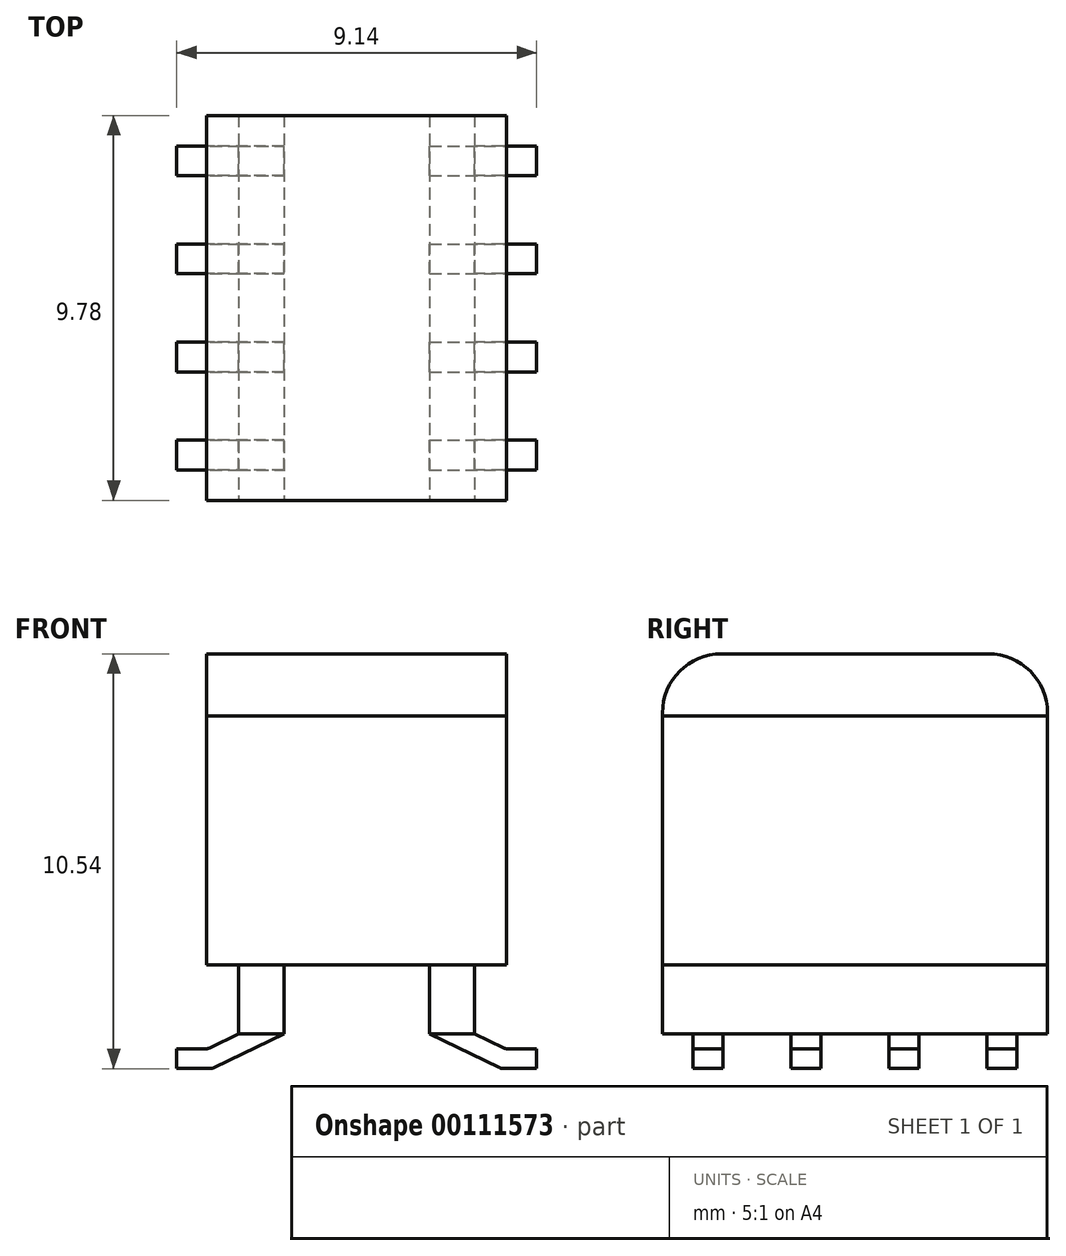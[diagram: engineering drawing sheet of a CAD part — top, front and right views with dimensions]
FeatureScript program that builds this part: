
annotation { "Feature Type Name" : "Feature", "Feature Type Description" : "" }
export const myFeature = defineFeature(function(context is Context, id is Id, definition is map)
    precondition{}
    {
        {
            var Q0;
            Q0=qCreatedBy(makeId("Top.planeOp"),FACE);
            var sketch = newSketch(context, id + "F0", { "sketchPlane" : qUnion([Q0])});
            skLineSegment(sketch, "E0.bottom", {"start": v(-3, 4.9) * mm, "end": v(-1.85, 4.9) * mm});
            skLineSegment(sketch, "E0.top", {"start": v(-3, -4.89) * mm, "end": v(-1.85, -4.89) * mm});
            skLineSegment(sketch, "E0.left", {"start": v(-3, 4.9) * mm, "end": v(-3, -4.89) * mm});
            skLineSegment(sketch, "E0.right", {"start": v(-1.85, 4.9) * mm, "end": v(-1.85, -4.89) * mm});
            skLineSegment(sketch, "E1.MirrorCS", {"start": v(3, -4.89) * mm, "end": v(1.85, -4.89) * mm});
            skLineSegment(sketch, "E2.MirrorCS", {"start": v(3, 4.9) * mm, "end": v(1.85, 4.9) * mm});
            skLineSegment(sketch, "E3.MirrorCS", {"start": v(3, 4.9) * mm, "end": v(3, -4.89) * mm});
            skLineSegment(sketch, "E4.MirrorCS", {"start": v(1.85, 4.9) * mm, "end": v(1.85, -4.89) * mm});
            skSolve(sketch);
        }
        {
            var Q0;
            Q0 = qSketchRegion(id + "F0", true);
            extrude(context, id + "F1", {"entities" : qUnion([Q0]), "depth" : 1.76 * mm});
        }
        {
            var Q0;
            Q0=makeQuery(id+"F1.opExtrude","CAP_FACE",FACE,{"disambiguationData":[OSD([sQuery(id+"F0.wireOp",EDGE,"E0.bottom"),sQuery(id+"F0.wireOp",EDGE,"E0.top"),sQuery(id+"F0.wireOp",EDGE,"E0.left"),sQuery(id+"F0.wireOp",EDGE,"E0.right")])],"isStart":false});
            var sketch = newSketch(context, id + "F2", { "sketchPlane" : qUnion([Q0])});
            skPoint(sketch, "E5.firstSnap0", {"position": v(-2.43, 4.9) * mm});
            skLineSegment(sketch, "E5.bottom", {"start": v(-3.81, 4.9) * mm, "end": v(3.81, 4.9) * mm});
            skLineSegment(sketch, "E5.top", {"start": v(-3.81, -4.89) * mm, "end": v(3.81, -4.89) * mm});
            skLineSegment(sketch, "E5.left", {"start": v(-3.81, 4.89) * mm, "end": v(-3.81, -4.89) * mm});
            skLineSegment(sketch, "E5.right", {"start": v(3.81, 4.9) * mm, "end": v(3.81, -4.89) * mm});
            skSolve(sketch);
        }
        {
            var Q0;
            Q0 = qSketchRegion(id + "F2", true);
            extrude(context, id + "F3", {"entities" : qUnion([Q0]), "depth" : 6.32 * mm});
        }
        {
            var Q0;
            Q0=makeQuery(id+"F3.opExtrude","CAP_FACE",FACE,{"disambiguationData":[OSD([sQuery(id+"F2.wireOp",EDGE,"E5.bottom"),sQuery(id+"F2.wireOp",EDGE,"E5.top"),sQuery(id+"F2.wireOp",EDGE,"E5.left"),sQuery(id+"F2.wireOp",EDGE,"E5.right")])],"isStart":false});
            var sketch = newSketch(context, id + "F4", { "sketchPlane" : qUnion([Q0])});
            skLineSegment(sketch, "E6.bottom", {"start": v(-3.81, 4.89) * mm, "end": v(3.81, 4.89) * mm});
            skLineSegment(sketch, "E6.top", {"start": v(-3.81, -4.89) * mm, "end": v(3.81, -4.89) * mm});
            skLineSegment(sketch, "E6.left", {"start": v(-3.81, 4.89) * mm, "end": v(-3.81, -4.89) * mm});
            skLineSegment(sketch, "E6.right", {"start": v(3.81, 4.89) * mm, "end": v(3.81, -4.89) * mm});
            skSolve(sketch);
        }
        {
            var Q0;
            Q0 = qSketchRegion(id + "F4", true);
            extrude(context, id + "F5", {"entities" : qUnion([Q0]), "depth" : 1.58 * mm});
        }
        {
            var Q0;
            Q0=makeQuery(id+"F5.opExtrude","SWEPT_FACE",FACE,{"disambiguationData":[OSD([sQuery(id+"F4.wireOp",EDGE,"E6.left")])]});
            var sketch = newSketch(context, id + "F6", { "sketchPlane" : qUnion([Q0])});
            skLineSegment(sketch, "E7.left", {"start": v(-4.89, 8.16) * mm, "end": v(-4.89, 8.08) * mm});
            skLineSegment(sketch, "E7.right", {"start": v(4.89, 8.16) * mm, "end": v(4.89, 8.08) * mm});
            skPoint(sketch, "E8.visualSharp", {"position": v(-4.89, 9.66) * mm});
            skArc(sketch, "E8.filletArc", {"start": v(-3.39, 9.66) * mm, "mid": v(-4.45, 9.22) * mm, "end": v(-4.89, 8.16) * mm});
            skPoint(sketch, "E9.visualSharp", {"position": v(4.89, 9.66) * mm});
            skArc(sketch, "E9.filletArc", {"start": v(4.89, 8.16) * mm, "mid": v(4.45, 9.22) * mm, "end": v(3.39, 9.66) * mm});
            skLineSegment(sketch, "E10", {"start": v(3.39, 9.66) * mm, "end": v(4.89, 9.66) * mm});
            skLineSegment(sketch, "E11", {"start": v(4.89, 9.66) * mm, "end": v(4.89, 8.16) * mm});
            skLineSegment(sketch, "E12", {"start": v(-3.39, 9.66) * mm, "end": v(-4.89, 9.66) * mm});
            skLineSegment(sketch, "E13", {"start": v(-4.89, 8.16) * mm, "end": v(-4.89, 9.66) * mm});
            skSolve(sketch);
        }
        {
            var Q0;
            Q0 = qSketchRegion(id + "F6", true);
            extrude(context, id + "F7", {"entities" : qUnion([Q0]), "operationType" : NewBodyOperationType.REMOVE, "oppositeDirection" : true, "depth" : 25 * mm});
        }
        {
            var Q0;
            Q0=makeQuery(id+"F1.opExtrude","SWEPT_FACE",FACE,{"disambiguationData":[OSD([sQuery(id+"F0.wireOp",EDGE,"E2.MirrorCS")])]});
            var sketch = newSketch(context, id + "F8", { "sketchPlane" : qUnion([Q0])});
            skLineSegment(sketch, "E14", {"start": v(-4.57, -0.38) * mm, "end": v(-4.57, -0.88) * mm});
            skLineSegment(sketch, "E15", {"start": v(-4.57, -0.88) * mm, "end": v(-3.72, -0.88) * mm});
            skLineSegment(sketch, "E16", {"start": v(-3.61, -0.85) * mm, "end": v(-1.85, 0) * mm});
            skLineSegment(sketch, "E17", {"start": v(-1.85, 0) * mm, "end": v(-3, 0) * mm});
            skLineSegment(sketch, "E18", {"start": v(-3, 0) * mm, "end": v(-3.73, -0.35) * mm});
            skLineSegment(sketch, "E19", {"start": v(-3.83, -0.38) * mm, "end": v(-4.57, -0.38) * mm});
            skPoint(sketch, "E20.visualSharp", {"position": v(-3.78, -0.38) * mm});
            skArc(sketch, "E20.filletArc", {"start": v(-3.83, -0.38) * mm, "mid": v(-3.78, -0.37) * mm, "end": v(-3.73, -0.35) * mm});
            skPoint(sketch, "E21.visualSharp", {"position": v(-3.66, -0.88) * mm});
            skArc(sketch, "E21.filletArc", {"start": v(-3.72, -0.88) * mm, "mid": v(-3.66, -0.87) * mm, "end": v(-3.61, -0.85) * mm});
            skArc(sketch, "E22.MirrorCS", {"start": v(3.83, -0.38) * mm, "mid": v(3.78, -0.37) * mm, "end": v(3.73, -0.35) * mm});
            skArc(sketch, "E23.MirrorCS", {"start": v(3.72, -0.88) * mm, "mid": v(3.66, -0.87) * mm, "end": v(3.61, -0.85) * mm});
            skLineSegment(sketch, "E24.MirrorCS", {"start": v(4.57, -0.88) * mm, "end": v(3.72, -0.88) * mm});
            skPoint(sketch, "E25.MirrorP", {"position": v(3.78, -0.38) * mm});
            skLineSegment(sketch, "E26.MirrorCS", {"start": v(3, 0) * mm, "end": v(3.73, -0.35) * mm});
            skLineSegment(sketch, "E27.MirrorCS", {"start": v(1.85, 0) * mm, "end": v(3, 0) * mm});
            skLineSegment(sketch, "E28.MirrorCS", {"start": v(3.61, -0.85) * mm, "end": v(1.85, 0) * mm});
            skPoint(sketch, "E29.MirrorP", {"position": v(3.66, -0.88) * mm});
            skLineSegment(sketch, "E30.MirrorCS", {"start": v(3.83, -0.38) * mm, "end": v(4.57, -0.38) * mm});
            skLineSegment(sketch, "E31.MirrorCS", {"start": v(4.57, -0.38) * mm, "end": v(4.57, -0.88) * mm});
            skSolve(sketch);
        }
        {
            var Q0;
            Q0 = qSketchRegion(id + "F8", true);
            extrude(context, id + "F9", {"entities" : qUnion([Q0]), "oppositeDirection" : true, "depth" : 9.78 * mm});
        }
        {
            var Q0;
            Q0=makeQuery(id+"F9.opExtrude","SWEPT_FACE",FACE,{"disambiguationData":[OSD([sQuery(id+"F8.wireOp",EDGE,"E14")])]});
            var sketch = newSketch(context, id + "F10", { "sketchPlane" : qUnion([Q0])});
            skLineSegment(sketch, "E32.bottom", {"start": v(-4.89, -0.87) * mm, "end": v(-4.11, -0.87) * mm});
            skLineSegment(sketch, "E32.top", {"start": v(-4.89, 0) * mm, "end": v(-4.11, 0) * mm});
            skLineSegment(sketch, "E32.left", {"start": v(-4.89, -0.87) * mm, "end": v(-4.89, 0) * mm});
            skLineSegment(sketch, "E32.right", {"start": v(-4.11, -0.87) * mm, "end": v(-4.11, 0) * mm});
            skLineSegment(sketch, "E33.bottom", {"start": v(-3.35, -0.87) * mm, "end": v(-1.62, -0.87) * mm});
            skLineSegment(sketch, "E33.top", {"start": v(-3.35, 0) * mm, "end": v(-1.62, 0) * mm});
            skLineSegment(sketch, "E33.left", {"start": v(-3.35, -0.87) * mm, "end": v(-3.35, 0) * mm});
            skLineSegment(sketch, "E33.right", {"start": v(-1.62, -0.87) * mm, "end": v(-1.62, 0) * mm});
            skLineSegment(sketch, "E34.bottom", {"start": v(-0.86, -0.87) * mm, "end": v(0, -0.87) * mm});
            skLineSegment(sketch, "E34.top", {"start": v(-0.86, 0) * mm, "end": v(0, 0) * mm});
            skLineSegment(sketch, "E34.left", {"start": v(-0.86, -0.87) * mm, "end": v(-0.86, 0) * mm});
            skLineSegment(sketch, "E34.right", {"start": v(0, -0.87) * mm, "end": v(0, 0) * mm});
            skLineSegment(sketch, "E35.MirrorCS", {"start": v(4.89, -0.87) * mm, "end": v(4.11, -0.87) * mm});
            skLineSegment(sketch, "E36.MirrorCS", {"start": v(4.89, 0) * mm, "end": v(4.11, 0) * mm});
            skLineSegment(sketch, "E37.MirrorCS", {"start": v(4.89, -0.87) * mm, "end": v(4.89, 0) * mm});
            skLineSegment(sketch, "E38.MirrorCS", {"start": v(4.11, -0.87) * mm, "end": v(4.11, 0) * mm});
            skLineSegment(sketch, "E39.MirrorCS", {"start": v(1.62, -0.87) * mm, "end": v(1.62, 0) * mm});
            skLineSegment(sketch, "E40.MirrorCS", {"start": v(3.35, -0.87) * mm, "end": v(3.35, 0) * mm});
            skLineSegment(sketch, "E41.MirrorCS", {"start": v(3.35, 0) * mm, "end": v(1.62, 0) * mm});
            skLineSegment(sketch, "E42.MirrorCS", {"start": v(3.35, -0.87) * mm, "end": v(1.62, -0.87) * mm});
            skLineSegment(sketch, "E43.MirrorCS", {"start": v(0.86, -0.87) * mm, "end": v(0, -0.87) * mm});
            skLineSegment(sketch, "E44.MirrorCS", {"start": v(0.86, 0) * mm, "end": v(0, 0) * mm});
            skLineSegment(sketch, "E45.MirrorCS", {"start": v(0.86, -0.87) * mm, "end": v(0.86, 0) * mm});
            skSolve(sketch);
        }
        {
            var Q0;
            Q0 = qSketchRegion(id + "F10", true);
            extrude(context, id + "F11", {"entities" : qUnion([Q0]), "operationType" : NewBodyOperationType.REMOVE, "oppositeDirection" : true, "depth" : 100 * mm});
        }
    });
